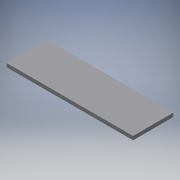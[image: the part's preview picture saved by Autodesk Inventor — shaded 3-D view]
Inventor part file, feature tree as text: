
AUTODESK INVENTOR PART (.ipt)
format: ipt  version: 2018.3 (Build 223284000, 284)  size: 91,648 bytes
history: native  units: mm
features: extrude x1, sketch x1
ambient origin geometry x8: Origin, YZ Plane, XZ Plane, XY Plane, X Axis, Y Axis, Z Axis, Center Point
bodies: Solid1 (feature_tree)
feature tree (2):
  extrude  "Extrusion1"  Depth=11.0mm
  sketch  "Sketch1"  dims[d0=34.5mm d1=11.0mm d2=1.0mm d3=0.0mm]
